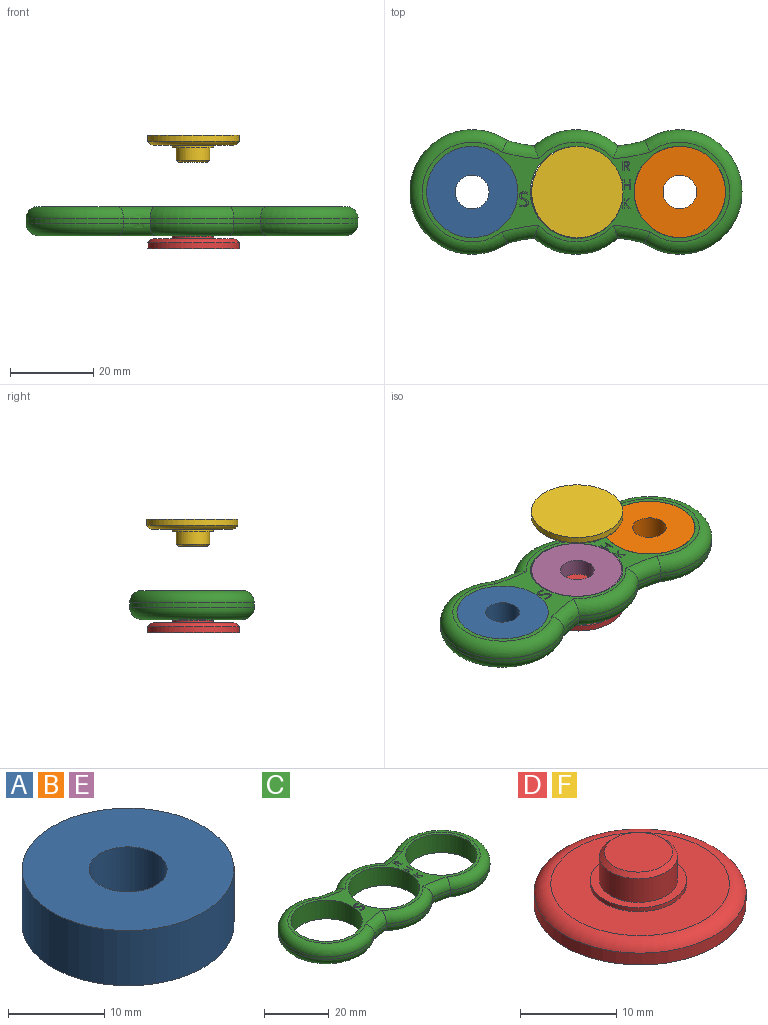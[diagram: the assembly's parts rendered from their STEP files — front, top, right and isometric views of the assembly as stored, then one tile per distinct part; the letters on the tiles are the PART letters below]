
ASSEMBLY  parts=6 mates=4
PART A: 4 faces, bbox 22x22x7 mm
  f0: cylinder r=4.05mm len=8.1mm, axis (0,0,-1), area 178.1mm2, adj f2,f3
  f1: cylinder r=11mm len=22mm, axis (0,0,-1), area 483.8mm2, adj f2,f3
  f2: plane 22x22mm, normal (0,0,1), area 328.6mm2, adj f0,f1
  f3: plane 22x22mm, normal (0,0,-1), area 328.6mm2, adj f0,f1
PART B: same geometry as A
PART C: 101 faces, bbox 82.5x32.5x7 mm
  f0: plane 74x24mm, normal (0,0,1), area 318.5mm2, adj f8,f9,f11,f21,f22,f23,f24,f25
  f1: cylinder r=35.11mm len=6.45mm, axis (0,0,-1), area 6.6mm2, adj f2,f10,f18,f22
  f2: cylinder r=15mm len=20.15mm, axis (0,0,-1), area 22.1mm2, adj f1,f3,f16,f24
  f3: cylinder r=35.11mm len=6.45mm, axis (0,0,-1), area 6.6mm2, adj f2,f4,f14,f26
  f4: cylinder r=15mm len=30mm, axis (0,0,-1), area 65.1mm2, adj f3,f5,f13,f28
  f5: cylinder r=35.11mm len=6.45mm, axis (0,0,-1), area 6.6mm2, adj f4,f6,f15,f27
  f6: cylinder r=15mm len=20.15mm, axis (0,0,-1), area 22.1mm2, adj f5,f7,f17,f25
  f7: cylinder r=35.11mm len=6.45mm, axis (0,0,-1), area 6.6mm2, adj f6,f10,f19,f23
  f8: cylinder r=11mm len=22mm, axis (0,0,-1), area 483.8mm2, adj f0,f12
  f9: cylinder r=11mm len=22mm, axis (0,0,-1), area 483.8mm2, adj f0,f12
  f10: cylinder r=15mm len=30mm, axis (0,0,-1), area 65.1mm2, adj f1,f7,f20,f21
  f11: cylinder r=11mm len=22mm, axis (0,0,-1), area 483.8mm2, adj f0,f12
  f12: plane 74x24mm, normal (0,0,-1), area 326.9mm2, adj f8,f9,f11,f13,f14,f15,f16,f17
  f13: torus R=12mm, axis (0,0,1), area 286.2mm2, adj f4,f12,f14,f15
  f14: torus R=38.11mm, axis (0,0,1), area 35.2mm2, adj f3,f12,f13,f16
  f15: torus R=38.11mm, axis (0,0,1), area 35.2mm2, adj f5,f12,f13,f17
  f16: torus R=12mm, axis (0,0,1), area 100.9mm2, adj f2,f12,f14,f18
  f17: torus R=12mm, axis (0,0,1), area 100.9mm2, adj f6,f12,f15,f19
  f18: torus R=38.11mm, axis (0,0,1), area 35.2mm2, adj f1,f12,f16,f20
  f19: torus R=38.11mm, axis (0,0,1), area 35.2mm2, adj f7,f12,f17,f20
  f20: torus R=12mm, axis (0,0,1), area 286.2mm2, adj f10,f12,f18,f19
  f21: torus R=12mm, axis (0,0,1), area 286.2mm2, adj f0,f10,f22,f23
  f22: torus R=38.11mm, axis (0,0,1), area 35.2mm2, adj f0,f1,f21,f24
  f23: torus R=38.11mm, axis (0,0,1), area 35.2mm2, adj f0,f7,f21,f25
  f24: torus R=12mm, axis (0,0,1), area 100.9mm2, adj f0,f2,f22,f26
  f25: torus R=12mm, axis (0,0,1), area 100.9mm2, adj f0,f6,f23,f27
  f26: torus R=38.11mm, axis (0,0,1), area 35.2mm2, adj f0,f3,f24,f28
  f27: torus R=38.11mm, axis (0,0,1), area 35.2mm2, adj f0,f5,f25,f28
  f28: torus R=12mm, axis (0,0,1), area 286.2mm2, adj f0,f4,f26,f27
  f29: plane 2.37x1mm, normal (-1,0,0), area 2.4mm2, adj f0,f30,f40,f41
  f30: plane 1x0.28mm, normal (0,-1,0), area 0.3mm2, adj f0,f29,f31,f41
  f31: plane 1.01x1mm, normal (1,0,0), area 1mm2, adj f0,f30,f32,f41
  f32: plane 1.25x1mm, normal (0,-1,0), area 1.2mm2, adj f0,f31,f33,f41
  f33: plane 1.01x1mm, normal (-1,0,0), area 1mm2, adj f0,f32,f34,f41
  f34: plane 1x0.28mm, normal (0,-1,0), area 0.3mm2, adj f0,f33,f35,f41
  f35: plane 2.37x1mm, normal (1,0,0), area 2.4mm2, adj f0,f34,f36,f41
  f36: plane 1x0.28mm, normal (0,1,0), area 0.3mm2, adj f0,f35,f37,f41
  f37: plane 1.11x1mm, normal (-1,0,0), area 1.1mm2, adj f0,f36,f38,f41
  f38: plane 1.25x1mm, normal (0,1,0), area 1.2mm2, adj f0,f37,f39,f41
  f39: plane 1.11x1mm, normal (1,0,0), area 1.1mm2, adj f0,f38,f40,f41
  f40: plane 1x0.28mm, normal (0,1,0), area 0.3mm2, adj f0,f29,f39,f41
  f41: plane 2.37x1.8mm, normal (0,0,1), area 1.6mm2, adj f29,f30,f31,f32,f33,f34,f35,f36
  f42: plane 1.34x1mm, normal (-0.8,-0.59,0), area 1.7mm2, adj f0,f43,f53,f54
  f43: plane 1.03x1mm, normal (-0.73,0.68,0), area 1.4mm2, adj f0,f42,f44,f54
  f44: plane 1x0.33mm, normal (0,-1,0), area 0.3mm2, adj f0,f43,f45,f54
  f45: plane 1.17x1.07mm, normal (0.74,-0.67,0), area 1.6mm2, adj f0,f44,f46,f54
  f46: plane 1.17x1mm, normal (-1,0,0), area 1.2mm2, adj f0,f45,f47,f54
  f47: plane 1x0.28mm, normal (0,-1,0), area 0.3mm2, adj f0,f46,f48,f54
  f48: plane 2.37x1mm, normal (1,0,0), area 2.4mm2, adj f0,f47,f49,f54
  f49: plane 1x0.28mm, normal (0,1,0), area 0.3mm2, adj f0,f48,f50,f54
  f50: plane 1x0.93mm, normal (-1,0,0), area 0.9mm2, adj f0,f49,f51,f54
  f51: plane 1x0.25mm, normal (-0.66,0.75,0), area 0.3mm2, adj f0,f50,f52,f54
  f52: plane 1.15x1mm, normal (0.8,0.6,0), area 1.4mm2, adj f0,f51,f53,f54
  f53: plane 1x0.32mm, normal (0,1,0), area 0.3mm2, adj f0,f42,f52,f54
  f54: plane 2.37x1.71mm, normal (0,0,1), area 1.5mm2, adj f42,f43,f44,f45,f46,f47,f48,f49
  f55: plane 1x0.49mm, normal (0,1,0), area 0.5mm2, adj f0,f56,f72,f73
  f56: plane 1x0.98mm, normal (0.86,0.5,0), area 1.1mm2, adj f0,f55,f57,f73
  f57: plane 1x0.33mm, normal (0,1,0), area 0.3mm2, adj f0,f56,f58,f73
  f58: plane 1.06x1mm, normal (-0.86,-0.52,0), area 1.2mm2, adj f0,f57,f59,f73
  f59: extruded ~1x0.63mm, area 0.9mm2, adj f0,f58,f60,f73
  f60: extruded ~1x0.5mm, area 0.6mm2, adj f0,f59,f61,f73
  f61: extruded ~1x0.64mm, area 0.7mm2, adj f0,f60,f62,f73
  f62: plane 1x0.65mm, normal (0,-1,0), area 0.6mm2, adj f0,f61,f63,f73
  f63: plane 2.37x1mm, normal (1,0,0), area 2.4mm2, adj f0,f62,f64,f73
  f64: plane 1x0.28mm, normal (0,1,0), area 0.3mm2, adj f0,f63,f72,f73
  f65: plane 1x0.9mm, normal (-1,0,0), area 0.9mm2, adj f66,f71,f73,f74
  f66: plane 1x0.36mm, normal (0,1,0), area 0.4mm2, adj f65,f67,f73,f74
  f67: extruded ~1x0.44mm, area 0.5mm2, adj f66,f68,f73,f74
  f68: extruded ~1x0.34mm, area 0.4mm2, adj f67,f69,f73,f74
  f69: extruded ~1x0.35mm, area 0.4mm2, adj f68,f70,f73,f74
  f70: extruded ~1x0.43mm, area 0.5mm2, adj f69,f71,f73,f74
  f71: plane 1x0.38mm, normal (0,-1,0), area 0.4mm2, adj f65,f70,f73,f74
  f72: plane 1x0.98mm, normal (-1,0,0), area 1mm2, adj f0,f55,f64,f73
  f73: plane 2.37x1.67mm, normal (0,0,1), area 1.7mm2, adj f55,f56,f57,f58,f59,f60,f61,f62
  f74: plane 0.94x0.9mm, normal (0,0,1), area 0.8mm2, adj f65,f66,f67,f68,f69,f70,f71
  f75: extruded ~2x0.59mm, area 1.3mm2, adj f0,f76,f99,f100
  f76: extruded ~2x0.76mm, area 1.8mm2, adj f0,f75,f77,f100
  f77: extruded ~2x0.49mm, area 1.1mm2, adj f0,f76,f78,f100
  f78: extruded ~2x0.23mm, area 0.6mm2, adj f0,f77,f79,f100
  f79: extruded ~2x0.3mm, area 0.6mm2, adj f0,f78,f80,f100
  f80: extruded ~2x0.39mm, area 0.9mm2, adj f0,f79,f81,f100
  f81: extruded ~2x0.51mm, area 1.1mm2, adj f0,f80,f82,f100
  f82: extruded ~2x0.85mm, area 1.7mm2, adj f0,f81,f83,f100
  f83: plane 2x0.36mm, normal (-0.94,0.34,0), area 0.8mm2, adj f0,f82,f84,f100
  f84: extruded ~2x0.96mm, area 2mm2, adj f0,f83,f85,f100
  f85: extruded ~2x0.81mm, area 1.7mm2, adj f0,f84,f86,f100
  f86: extruded ~2x0.65mm, area 1.5mm2, adj f0,f85,f87,f100
  f87: extruded ~2x0.63mm, area 1.4mm2, adj f0,f86,f88,f100
  f88: extruded ~2x0.7mm, area 1.6mm2, adj f0,f87,f89,f100
  f89: extruded ~2x0.52mm, area 1.1mm2, adj f0,f88,f90,f100
  f90: extruded ~2x0.25mm, area 0.7mm2, adj f0,f89,f91,f100
  f91: extruded ~2x0.3mm, area 0.6mm2, adj f0,f90,f92,f100
  f92: extruded ~2x0.43mm, area 1mm2, adj f0,f91,f93,f100
  f93: extruded ~2x0.62mm, area 1.3mm2, adj f0,f92,f94,f100
  f94: extruded ~2x0.5mm, area 1mm2, adj f0,f93,f95,f100
  f95: extruded ~2x0.47mm, area 1mm2, adj f0,f94,f96,f100
  f96: plane 2x0.39mm, normal (1,0,0), area 0.8mm2, adj f0,f95,f97,f100
  f97: extruded ~2x0.96mm, area 2mm2, adj f0,f96,f98,f100
  f98: extruded ~2x0.91mm, area 1.9mm2, adj f0,f97,f99,f100
  f99: extruded ~2x0.72mm, area 1.7mm2, adj f0,f75,f98,f100
  f100: plane 3.61x2.21mm, normal (0,0,1), area 2.9mm2, adj f75,f76,f77,f78,f79,f80,f81,f82
PART D: 9 faces, bbox 24.4x24.4x6.5 mm
  f0: plane 18.54x18.54mm, normal (0,0,1), area 191.3mm2, adj f1,f5
  f1: cylinder r=5mm len=10mm, axis (0,0,-1), area 15.7mm2, adj f0,f2
  f2: plane 10x10mm, normal (0,0,1), area 27mm2, adj f1,f4
  f3: plane 7.1x7.1mm, normal (0,0,1), area 39.6mm2, adj f6
  f4: cylinder r=4.05mm len=8.1mm, axis (0,0,-1), area 76.3mm2, adj f2,f6
  f5: torus R=9.27mm, axis (0,0,-1), area 134.5mm2, adj f0,f7
  f6: cone r=3.55mm half-angle=45deg, axis (0,0,-1), area 16.9mm2, adj f3,f4
  f7: cylinder r=11mm len=22mm, axis (0,0,1), area 103.7mm2, adj f5,f8
  f8: plane 22x22mm, normal (0,0,-1), area 380.1mm2, adj f7
PART E: same geometry as A
PART F: same geometry as D
PLACE A t=(-25.23,0.2,-1.09)mm
PLACE B t=(24.77,0.2,-1.09)mm
PLACE C t=(-0.23,0.2,-1.09)mm
PLACE D t=(0,0,-2.8)mm
PLACE E t=(0,0,-1.09)mm
PLACE F rot(axis=(1,0,0),180deg) t=(0,0,21.61)mm
MATE cylindrical E.f0 <-> F.f4  axis (0,0,1) through (0,0,5.91)mm
MATE slider B.f1 <-> C.f10  axis (0,0,-1) through (24.77,0.2,-1.09)mm
MATE cylindrical D.f4 <-> E.f0  axis (0,0,1) through (0,0,2.2)mm
MATE slider A.f1 <-> C.f4  axis (0,0,-1) through (-25.23,0.2,-1.09)mm
